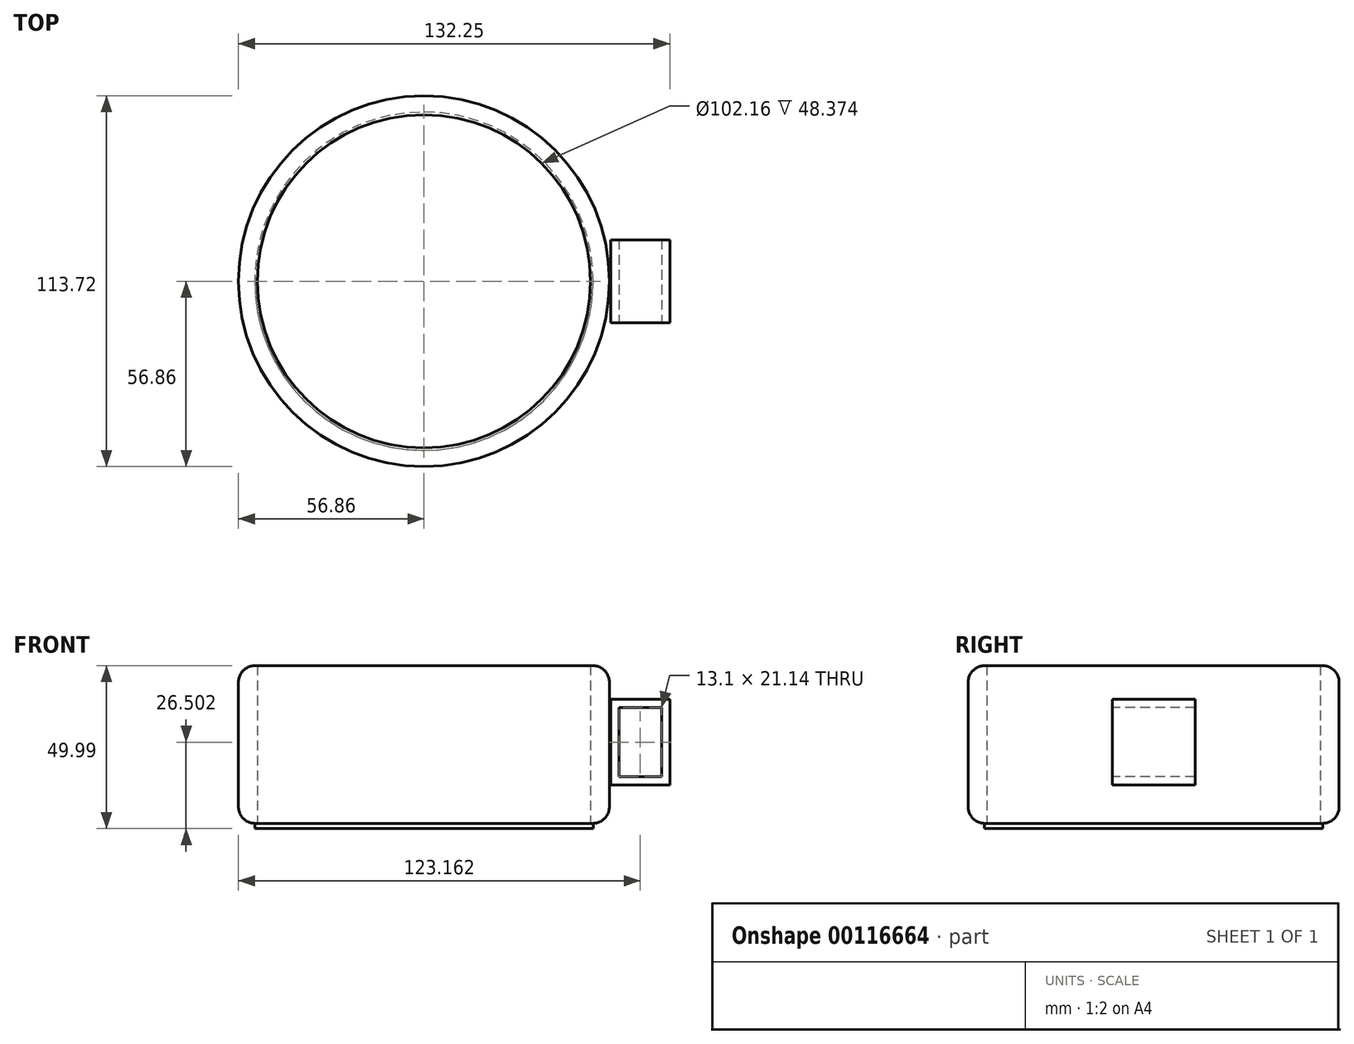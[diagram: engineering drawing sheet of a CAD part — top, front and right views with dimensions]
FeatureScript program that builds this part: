
annotation { "Feature Type Name" : "Feature", "Feature Type Description" : "" }
export const myFeature = defineFeature(function(context is Context, id is Id, definition is map)
    precondition{}
    {
        {
            var Q0;
            Q0=qCreatedBy(makeId("Top.planeOp"),FACE);
            var sketch = newSketch(context, id + "F0", { "sketchPlane" : qUnion([Q0])});
            skCircle(sketch, "E0", {"center": v(0, 0) * mm, "radius": 56.86 * mm});
            skCircle(sketch, "E1", {"center": v(0, 0) * mm, "radius": 51.08 * mm});
            skSolve(sketch);
        }
        {
            var Q0;
            Q0 = qSketchRegion(id + "F0", true);
            extrude(context, id + "F1", {"entities" : qUnion([Q0]), "depth" : 48.37 * mm});
        }
        {
            var Q0;
            Q0=qCreatedBy(makeId("Top.planeOp"),FACE);
            var sketch = newSketch(context, id + "F2", { "sketchPlane" : qUnion([Q0])});
            skCircle(sketch, "E2", {"center": v(0, 0) * mm, "radius": 51.88 * mm});
            skSolve(sketch);
        }
        {
            var Q0;
            Q0 = qSketchRegion(id + "F2", true);
            extrude(context, id + "F3", {"entities" : qUnion([Q0]), "operationType" : NewBodyOperationType.ADD, "oppositeDirection" : true, "depth" : 1.62 * mm});
        }
        {
            var Q0;
            Q0=qCreatedBy(makeId("Front.planeOp"),FACE);
            var sketch = newSketch(context, id + "F4", { "sketchPlane" : qUnion([Q0])});
            skLineSegment(sketch, "E3", {"start": v(57.21, 38) * mm, "end": v(75.4, 38) * mm});
            skLineSegment(sketch, "E4", {"start": v(75.4, 38) * mm, "end": v(75.4, 11.77) * mm});
            skLineSegment(sketch, "E5", {"start": v(75.4, 11.77) * mm, "end": v(56.62, 11.77) * mm});
            skLineSegment(sketch, "E6.top", {"start": v(57.21, 11.77) * mm, "end": v(75.4, 11.77) * mm});
            skLineSegment(sketch, "E6.left", {"start": v(57.21, 38) * mm, "end": v(57.21, 11.77) * mm});
            skSolve(sketch);
        }
        {
            var Q0;
            Q0 = qSketchRegion(id + "F4", true);
            extrude(context, id + "F5", {"entities" : qUnion([Q0]), "endBound" : BoundingType.SYMMETRIC, "oppositeDirection" : true, "depth" : 25.4 * mm});
        }
        {
            var Q0;
            Q0=makeQuery(id+"F5.opExtrude","CAP_FACE",FACE,{"disambiguationData":[OSD([sQuery(id+"F4.wireOp",EDGE,"E3"),sQuery(id+"F4.wireOp",EDGE,"E6.top"),sQuery(id+"F4.wireOp",EDGE,"E6.left"),sQuery(id+"F4.wireOp",EDGE,"E4")])],"isStart":true});
            var Q1;
            Q1=makeQuery(id+"F5.opExtrude","CAP_FACE",FACE,{"disambiguationData":[OSD([sQuery(id+"F4.wireOp",EDGE,"E3"),sQuery(id+"F4.wireOp",EDGE,"E6.top"),sQuery(id+"F4.wireOp",EDGE,"E6.left"),sQuery(id+"F4.wireOp",EDGE,"E4")])],"isStart":false});
            shell(context, id + "F6", {"entities" : qUnion([Q0, Q1]), "thickness" : 2.54 * mm});
        }
        {
            var Q0;
            Q0=makeQuery(id+"F1.opExtrude","CAP_EDGE",EDGE,{"disambiguationData":[OSD([sQuery(id+"F0.wireOp",EDGE,"E0")])],"isStart":false});
            fillet(context, id + "F7", {"entities" : qUnion([Q0]), "radius" : 5.08 * mm, "tangentPropagation" : true, "allowEdgeOverflow" : false});
        }
        {
            var Q0;
            Q0=makeQuery(id+"F1.opExtrude","CAP_EDGE",EDGE,{"disambiguationData":[OSD([sQuery(id+"F0.wireOp",EDGE,"E0")])],"isStart":true});
            fillet(context, id + "F8", {"entities" : qUnion([Q0]), "radius" : 5.08 * mm, "tangentPropagation" : true, "allowEdgeOverflow" : false});
        }
    });
